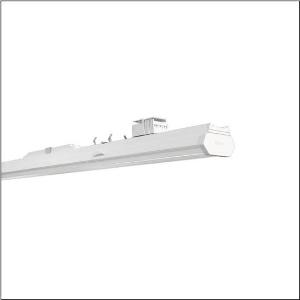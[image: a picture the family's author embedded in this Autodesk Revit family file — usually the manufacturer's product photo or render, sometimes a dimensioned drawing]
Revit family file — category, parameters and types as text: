
# Revit family: licross_11_protected_extreme_mo_51td1bdn49xge
name_source: partatom
category: Lighting Fixtures
units: mm (PartAtom-declared; Revit-internal decimal feet)

## family parameters
Cut with Voids When Loaded = No
Host = Face
Light Source = No
Part Type = Normal
Room Calculation Point = No
Round Connector Dimension = Use Diameter
Shared = No

## types (1)
- --- (1 x LED, 9370 lm, 57.1 W, 4000K)
    Apparent Load = 57 VA
    CIE Flux Codes = 54 82 95 97 100
    Color Rendering = 80
    Color Temperature = 4000K
    Default Elevation = 1800 mm
    Description = Licross 11 Protected extreme MO, luminaire insert, of sheet steel, galvanised, coil coated, white, length: 1.500mm, width: 90mm, height: 101mm, LED rated luminous flux: 9.370lm, light colour: 840, SDCM (Standard Deviation of Colour Matching)MacAdam ≤ 2 SDCM (initial), control gear: DALI 2, with plug, 5-pole, with phase selection, mains connection: 220..240V, AC, 50/60Hz, rated input power: 57W, internal wiring halogen-free, primary optical cover: cover, of PMMA, light emission: direct distribution, primary light characteristic: symmetric, protection rating (complete): IP54, insulation class (complete): insulation class I (protective earthing), certification: CE, ENEC, VDE, UKCA, protection symbol: D if used in an environment with non-conductive dust loads with corresponding accessories, impact resistance: IK06, permissible ambient temperature for indoor applications: -40..+45°C, corresponds to IFS (International Featured Standards) requirements for safety and quality in the food industry, reducing of maximum allowable ambient temperature of 5°C with ceiling mounting, LABS conformity tested according to VDMA 24364:2018-05, The light source and the operating device comply with the requirements of the Ecodesign Regulation (EU) 2019/2020 and are replaceable in accordance with this regulation, packaging unit: 1 piece
    Height = 92 mm
    Lamp = 1 x LED
    Lamp Light Flux = 9370 lm
    Lamp Power = 57.1 W
    Lamp count = 1
    Length = 1500 mm
    Luminous efficacy = 164 lm/W
    Manufacturer = Siteco
    ModVariant = No
    Model = 51TD1BDN49XGE
    Mounting Place = Ceiling
    Mounting Type = Pendant
    Number of Poles = 1
    OnlyDefault = Yes
    Power Factor = 1
    Product Name = Licross 11 Protected extreme MO
    Product group = luminaire insert | ceiling pendant
    ProductGroupID = 901
    Protection Class = Protection class I
    Protection Degree = IP 54
    RLX_Detail_Level = 1
    RLX_Emergency_Light_Flux = 0 lm
    RLX_Emergency_Type = 0
    RLX_Emergency_Type_DB = No
    RlxData = <blob elided: 24677 chars, md5=9288761d>
    Socket = socket
    Standby Power = 0 W
    System Light Flux = 9370 lm
    System Power = 57 W
    Type Comments = factory setting: luminous flux: 100 % | dim-lin: 254 | 378 mA
    Type Image = l_1256145.jpg
    URL = http://relux.com
    VarID = @adj_089343
    Voltage = 0 V
    Weight = 0.00 kg
    Width = 88 mm

## geometry (parser evidence)
native form markers: Blend x4, Sweep x10
no freeform markers — native parametric forms only
